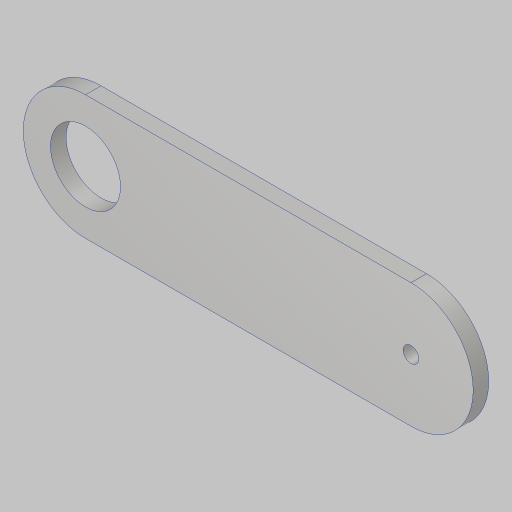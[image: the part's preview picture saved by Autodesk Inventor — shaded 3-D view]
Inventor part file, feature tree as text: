
AUTODESK INVENTOR PART (.ipt)
format: ipt  version: 2023.5 (Build 275446000, 446)  size: 109,056 bytes
history: native  units: in
note: dims shown in document units (in); Inventor stores cm internally (conversion verified against a paired STEP export)
features: extrude x1, sketch x1
ambient origin geometry x8: Origin, YZ Plane, XZ Plane, XY Plane, X Axis, Y Axis, Z Axis, Center Point
bodies: Solid1 (feature_tree)
feature tree (2):
  extrude  "Extrusion1"  Depth=0.25in
  sketch  "Sketch1"  dims[d0=1.125in d1=0.25in d2=2.0in d3=5.235in d4=0.25in d5=0.0in]
